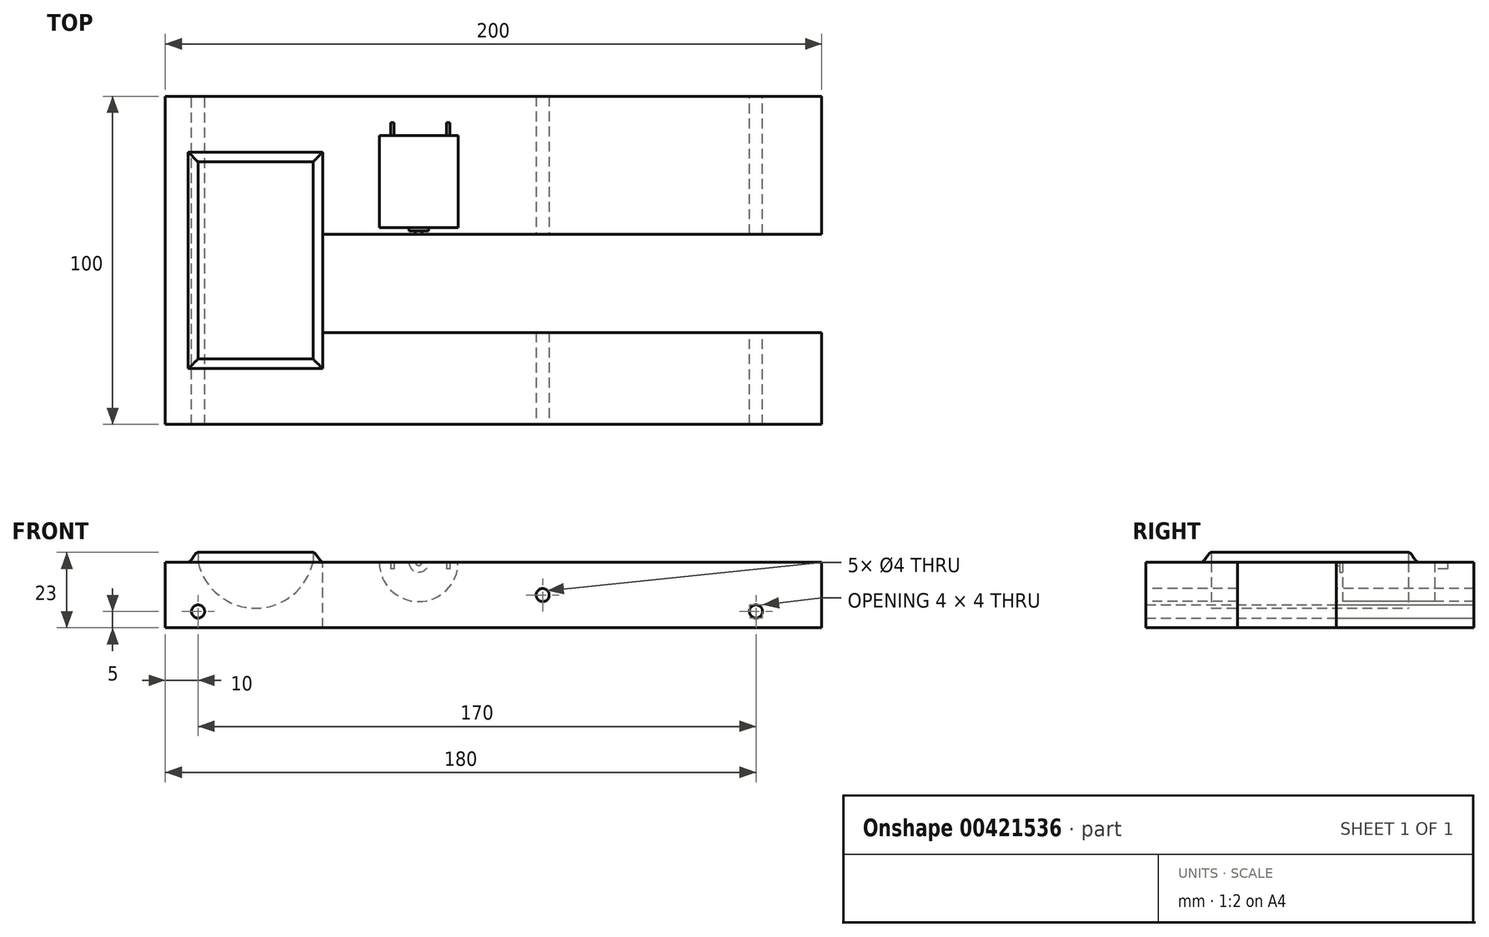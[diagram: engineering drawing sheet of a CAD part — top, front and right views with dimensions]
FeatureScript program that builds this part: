
annotation { "Feature Type Name" : "Feature", "Feature Type Description" : "" }
export const myFeature = defineFeature(function(context is Context, id is Id, definition is map)
    precondition{}
    {
        {
            var Q0;
            Q0=qCreatedBy(makeId("Right.planeOp"),FACE);
            var sketch = newSketch(context, id + "F0", { "sketchPlane" : qUnion([Q0])});
            skLineSegment(sketch, "E0.bottom", {"start": v(50, 10) * mm, "end": v(-50, 10) * mm});
            skLineSegment(sketch, "E0.top", {"start": v(50, -10) * mm, "end": v(-50, -10) * mm});
            skLineSegment(sketch, "E0.left", {"start": v(50, 10) * mm, "end": v(50, -10) * mm});
            skLineSegment(sketch, "E0.right", {"start": v(-50, 10) * mm, "end": v(-50, -10) * mm});
            skPoint(sketch, "E0.middle", {"position": v(0, 0) * mm});
            skSolve(sketch);
        }
        {
            var Q0;
            Q0 = qSketchRegion(id + "F0", true);
            extrude(context, id + "F1", {"entities" : qUnion([Q0]), "endBound" : BoundingType.SYMMETRIC, "depth" : 200 * mm});
        }
        {
            var Q0;
            Q0=qCreatedBy(makeId("Front.planeOp"),FACE);
            var sketch = newSketch(context, id + "F2", { "sketchPlane" : qUnion([Q0])});
            skLineSegment(sketch, "E1.bottom", {"start": v(-100, 10) * mm, "end": v(100, 10) * mm, "construction": true});
            skLineSegment(sketch, "E1.top", {"start": v(-100, -10) * mm, "end": v(100, -10) * mm, "construction": true});
            skLineSegment(sketch, "E1.left", {"start": v(-100, 10) * mm, "end": v(-100, -10) * mm, "construction": true});
            skLineSegment(sketch, "E1.right", {"start": v(100, 10) * mm, "end": v(100, -10) * mm, "construction": true});
            skPoint(sketch, "E1.middle", {"position": v(0, 0) * mm});
            skLineSegment(sketch, "E2", {"start": v(-90, 10) * mm, "end": v(-55, 10) * mm});
            skArc(sketch, "E3", {"start": v(-90, 10) * mm, "mid": v(-72.5, -4) * mm, "end": v(-55, 10) * mm});
            skSolve(sketch);
        }
        {
            var Q0;
            Q0 = qSketchRegion(id + "F2", true);
            extrude(context, id + "F3", {"entities" : qUnion([Q0]), "operationType" : NewBodyOperationType.REMOVE, "endBound" : BoundingType.SYMMETRIC, "depth" : 60 * mm});
        }
        {
            var Q0;
            Q0=makeQuery(id+"F1.opExtrude","SWEPT_FACE",FACE,{"disambiguationData":[OSD([sQuery(id+"F0.wireOp",EDGE,"E0.left")])]});
            var sketch = newSketch(context, id + "F4", { "sketchPlane" : qUnion([Q0])});
            skCircle(sketch, "E4", {"center": v(-80, -5) * mm, "radius": 2 * mm});
            skCircle(sketch, "E5", {"center": v(90, -5) * mm, "radius": 2 * mm});
            skSolve(sketch);
        }
        {
            var Q0;
            Q0 = qSketchRegion(id + "F4", true);
            extrude(context, id + "F5", {"entities" : qUnion([Q0]), "operationType" : NewBodyOperationType.REMOVE, "endBound" : BoundingType.THROUGH_ALL, "oppositeDirection" : true, "depth" : 25 * mm});
        }
        {
            var Q0;
            Q0=makeQuery(id+"F1.opExtrude","SWEPT_FACE",FACE,{"disambiguationData":[OSD([sQuery(id+"F0.wireOp",EDGE,"E0.bottom")])]});
            var sketch = newSketch(context, id + "F6", { "sketchPlane" : qUnion([Q0])});
            skLineSegment(sketch, "E6.bottom", {"start": v(-90, 30) * mm, "end": v(-55, 30) * mm});
            skLineSegment(sketch, "E6.top", {"start": v(-90, -30) * mm, "end": v(-55, -30) * mm});
            skLineSegment(sketch, "E6.left", {"start": v(-90, 30) * mm, "end": v(-90, -30) * mm});
            skLineSegment(sketch, "E6.right", {"start": v(-55, 30) * mm, "end": v(-55, -30) * mm});
            skSolve(sketch);
        }
        {
            var Q0;
            Q0=makeQuery(id+"F3.boolean.opBoolean","COPY",FACE,{"derivedFrom":makeQuery(id+"F3.opExtrude","CAP_FACE",FACE,{"disambiguationData":[OSD([sQuery(id+"F2.wireOp",EDGE,"E2"),sQuery(id+"F2.wireOp",EDGE,"E3")])],"isStart":true})});
            var sketch = newSketch(context, id + "F7", { "sketchPlane" : qUnion([Q0])});
            skLineSegment(sketch, "E7", {"start": v(-90, 10) * mm, "end": v(-90, 13) * mm});
            skLineSegment(sketch, "E8", {"start": v(-93, 10) * mm, "end": v(-90, 10) * mm});
            skFitSpline(sketch, "E9", {"points": [v(-93, 10) * mm, v(-90, 13) * mm], "startDerivative": vector(4.05, 1.57) * mm, "endDerivative": vector(3.33, -0.05) * mm});
            skSolve(sketch);
        }
        {
            var Q0;
            Q0 = qSketchRegion(id + "F7", true);
            var Q1;
            Q1 = qConstructionFilter(qBodyType(qCreatedBy(id + "F6" ,EDGE), BodyType.WIRE), ConstructionObject.NO);
            sweep(context, id + "F8", {"operationType" : NewBodyOperationType.ADD, "profiles" : qUnion([Q0]), "path" : qUnion([Q1])});
        }
        {
            var Q0;
            Q0=qCreatedBy(makeId("Front.planeOp"),FACE);
            cPlane(context, id + "F9", {"entities" : qUnion([Q0]), "cplaneType" : CPlaneType.OFFSET, "offset" : 10 * mm, "oppositeDirection" : true, "width" : 150 * mm, "height" : 150 * mm});
        }
        {
            var Q0;
            Q0=qCreatedBy(id+"F9.planeOp",FACE);
            var sketch = newSketch(context, id + "F10", { "sketchPlane" : qUnion([Q0])});
            skLineSegment(sketch, "E10.bottom", {"start": v(-100, 10) * mm, "end": v(100, 10) * mm, "construction": true});
            skLineSegment(sketch, "E10.top", {"start": v(-100, -10) * mm, "end": v(100, -10) * mm, "construction": true});
            skLineSegment(sketch, "E10.left", {"start": v(-100, 10) * mm, "end": v(-100, -10) * mm, "construction": true});
            skLineSegment(sketch, "E10.right", {"start": v(100, 10) * mm, "end": v(100, -10) * mm, "construction": true});
            skPoint(sketch, "E10.middle", {"position": v(0, 0) * mm});
            skArc(sketch, "E11", {"start": v(-34.77, 10) * mm, "mid": v(-22.77, -2) * mm, "end": v(-10.77, 10) * mm});
            skLineSegment(sketch, "E12", {"start": v(-34.77, 10) * mm, "end": v(-10.77, 10) * mm});
            skSolve(sketch);
        }
        {
            var Q0;
            Q0 = qSketchRegion(id + "F10", true);
            extrude(context, id + "F11", {"entities" : qUnion([Q0]), "operationType" : NewBodyOperationType.REMOVE, "oppositeDirection" : true, "depth" : 28 * mm});
        }
        {
            var Q0;
            Q0=makeQuery(id+"F11.boolean.opBoolean","COPY",FACE,{"derivedFrom":makeQuery(id+"F11.opExtrude","CAP_FACE",FACE,{"disambiguationData":[OSD([sQuery(id+"F10.wireOp",EDGE,"E11"),sQuery(id+"F10.wireOp",EDGE,"E12")])],"isStart":false})});
            var sketch = newSketch(context, id + "F12", { "sketchPlane" : qUnion([Q0])});
            skPoint(sketch, "E13", {"position": v(-30.77, 10) * mm});
            skPoint(sketch, "E14", {"position": v(-13.77, 10) * mm});
            skLineSegment(sketch, "E15.bottom", {"start": v(-30.27, 12) * mm, "end": v(-31.27, 12) * mm});
            skLineSegment(sketch, "E15.top", {"start": v(-30.27, 8) * mm, "end": v(-31.27, 8) * mm});
            skLineSegment(sketch, "E15.left", {"start": v(-30.27, 12) * mm, "end": v(-30.27, 8) * mm});
            skLineSegment(sketch, "E15.right", {"start": v(-31.27, 12) * mm, "end": v(-31.27, 8) * mm});
            skLineSegment(sketch, "E16.bottom", {"start": v(-13.27, 12) * mm, "end": v(-14.27, 12) * mm});
            skLineSegment(sketch, "E16.top", {"start": v(-13.27, 8) * mm, "end": v(-14.27, 8) * mm});
            skLineSegment(sketch, "E16.left", {"start": v(-13.27, 12) * mm, "end": v(-13.27, 8) * mm});
            skLineSegment(sketch, "E16.right", {"start": v(-14.27, 12) * mm, "end": v(-14.27, 8) * mm});
            skSolve(sketch);
        }
        {
            var Q0;
            Q0 = qSketchRegion(id + "F12", true);
            extrude(context, id + "F13", {"entities" : qUnion([Q0]), "operationType" : NewBodyOperationType.REMOVE, "oppositeDirection" : true, "depth" : 4 * mm});
        }
        {
            var Q0;
            Q0=makeQuery(id+"F11.boolean.opBoolean","COPY",FACE,{"derivedFrom":makeQuery(id+"F11.opExtrude","CAP_FACE",FACE,{"disambiguationData":[OSD([sQuery(id+"F10.wireOp",EDGE,"E11"),sQuery(id+"F10.wireOp",EDGE,"E12")])],"isStart":true})});
            var sketch = newSketch(context, id + "F14", { "sketchPlane" : qUnion([Q0])});
            skCircle(sketch, "E17", {"center": v(22.77, 10) * mm, "radius": 3 * mm});
            skSolve(sketch);
        }
        {
            var Q0;
            Q0 = qSketchRegion(id + "F14", true);
            extrude(context, id + "F15", {"entities" : qUnion([Q0]), "operationType" : NewBodyOperationType.REMOVE, "oppositeDirection" : true, "depth" : 1 * mm});
        }
        {
            var Q0;
            Q0=makeQuery(id+"F15.boolean.opBoolean","COPY",FACE,{"derivedFrom":makeQuery(id+"F15.opExtrude","CAP_FACE",FACE,{"disambiguationData":[OSD([sQuery(id+"F14.wireOp",EDGE,"E17")])],"isStart":false})});
            var sketch = newSketch(context, id + "F16", { "sketchPlane" : qUnion([Q0])});
            skCircle(sketch, "E18", {"center": v(22.77, 10) * mm, "radius": 1 * mm});
            skSolve(sketch);
        }
        {
            var Q0;
            Q0 = qSketchRegion(id + "F16", true);
            extrude(context, id + "F17", {"entities" : qUnion([Q0]), "operationType" : NewBodyOperationType.REMOVE, "oppositeDirection" : true, "depth" : 1 * mm});
        }
        {
            var Q0;
            Q0=makeQuery(id+"F1.opExtrude","SWEPT_FACE",FACE,{"disambiguationData":[OSD([sQuery(id+"F0.wireOp",EDGE,"E0.bottom")])]});
            var sketch = newSketch(context, id + "F18", { "sketchPlane" : qUnion([Q0])});
            skLineSegment(sketch, "E19.bottom", {"start": v(-52, 8) * mm, "end": v(100, 8) * mm});
            skLineSegment(sketch, "E19.top", {"start": v(-52, -22) * mm, "end": v(100, -22) * mm});
            skLineSegment(sketch, "E19.left", {"start": v(-52, 8) * mm, "end": v(-52, -22) * mm});
            skLineSegment(sketch, "E19.right", {"start": v(100, 8) * mm, "end": v(100, -22) * mm});
            skSolve(sketch);
        }
        {
            var Q0;
            Q0 = qSketchRegion(id + "F18", true);
            extrude(context, id + "F19", {"entities" : qUnion([Q0]), "operationType" : NewBodyOperationType.REMOVE, "endBound" : BoundingType.THROUGH_ALL, "oppositeDirection" : true, "depth" : 25 * mm});
        }
        {
            var Q0;
            Q0=makeQuery(id+"F1.opExtrude","SWEPT_FACE",FACE,{"disambiguationData":[OSD([sQuery(id+"F0.wireOp",EDGE,"E0.right")])]});
            var sketch = newSketch(context, id + "F20", { "sketchPlane" : qUnion([Q0])});
            skCircle(sketch, "E20", {"center": v(15, 0) * mm, "radius": 2 * mm});
            skSolve(sketch);
        }
        {
            var Q0;
            Q0 = qSketchRegion(id + "F20", true);
            extrude(context, id + "F21", {"entities" : qUnion([Q0]), "operationType" : NewBodyOperationType.REMOVE, "endBound" : BoundingType.THROUGH_ALL, "oppositeDirection" : true, "depth" : 25 * mm});
        }
    });
